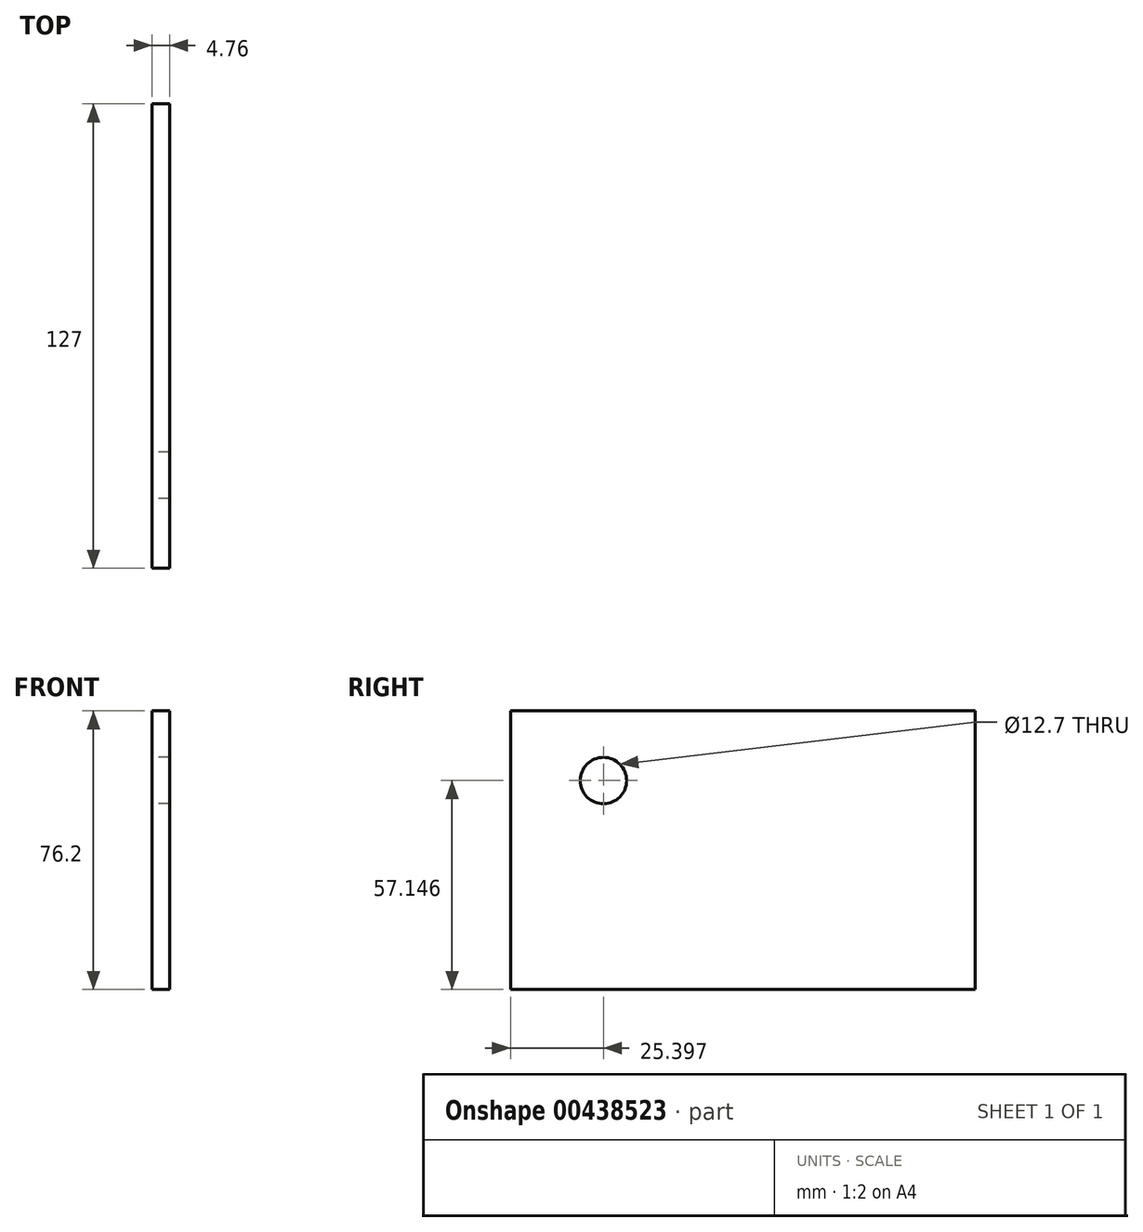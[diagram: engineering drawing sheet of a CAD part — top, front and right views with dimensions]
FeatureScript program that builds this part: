
annotation { "Feature Type Name" : "Feature", "Feature Type Description" : "" }
export const myFeature = defineFeature(function(context is Context, id is Id, definition is map)
    precondition{}
    {
        {
            var Q0;
            Q0=qCreatedBy(makeId("Right.planeOp"),FACE);
            var sketch = newSketch(context, id + "F0", { "sketchPlane" : qUnion([Q0])});
            skLineSegment(sketch, "E0.bottom", {"start": v(-83.55, 12.74) * mm, "end": v(43.45, 12.74) * mm});
            skLineSegment(sketch, "E0.top", {"start": v(-83.55, -63.46) * mm, "end": v(43.45, -63.46) * mm});
            skLineSegment(sketch, "E0.left", {"start": v(-83.55, 12.74) * mm, "end": v(-83.55, -63.46) * mm});
            skLineSegment(sketch, "E0.right", {"start": v(43.45, 12.74) * mm, "end": v(43.45, -63.46) * mm});
            skCircle(sketch, "E1", {"center": v(-58.15, -6.31) * mm, "radius": 6.35 * mm});
            skPoint(sketch, "E1.first.point", {"position": v(-62.98, -2.19) * mm});
            skPoint(sketch, "E1.second.point", {"position": v(-51.83, -6.85) * mm});
            skPoint(sketch, "E1.third.point", {"position": v(-57.47, 0) * mm});
            skSolve(sketch);
        }
        {
            var Q0;
            Q0=makeQuery(id+"F0.imprint","IMPRINT",FACE,{"disambiguationData":[TD([[makeQuery(id+"F0.imprint","IMPRINT",EDGE,{"derivedFrom":sQuery(id+"F0.wireOp",EDGE,"E0.bottom")}),-1.0]])]});
            extrude(context, id + "F1", {"entities" : qUnion([Q0]), "depth" : 4.76 * mm});
        }
    });
